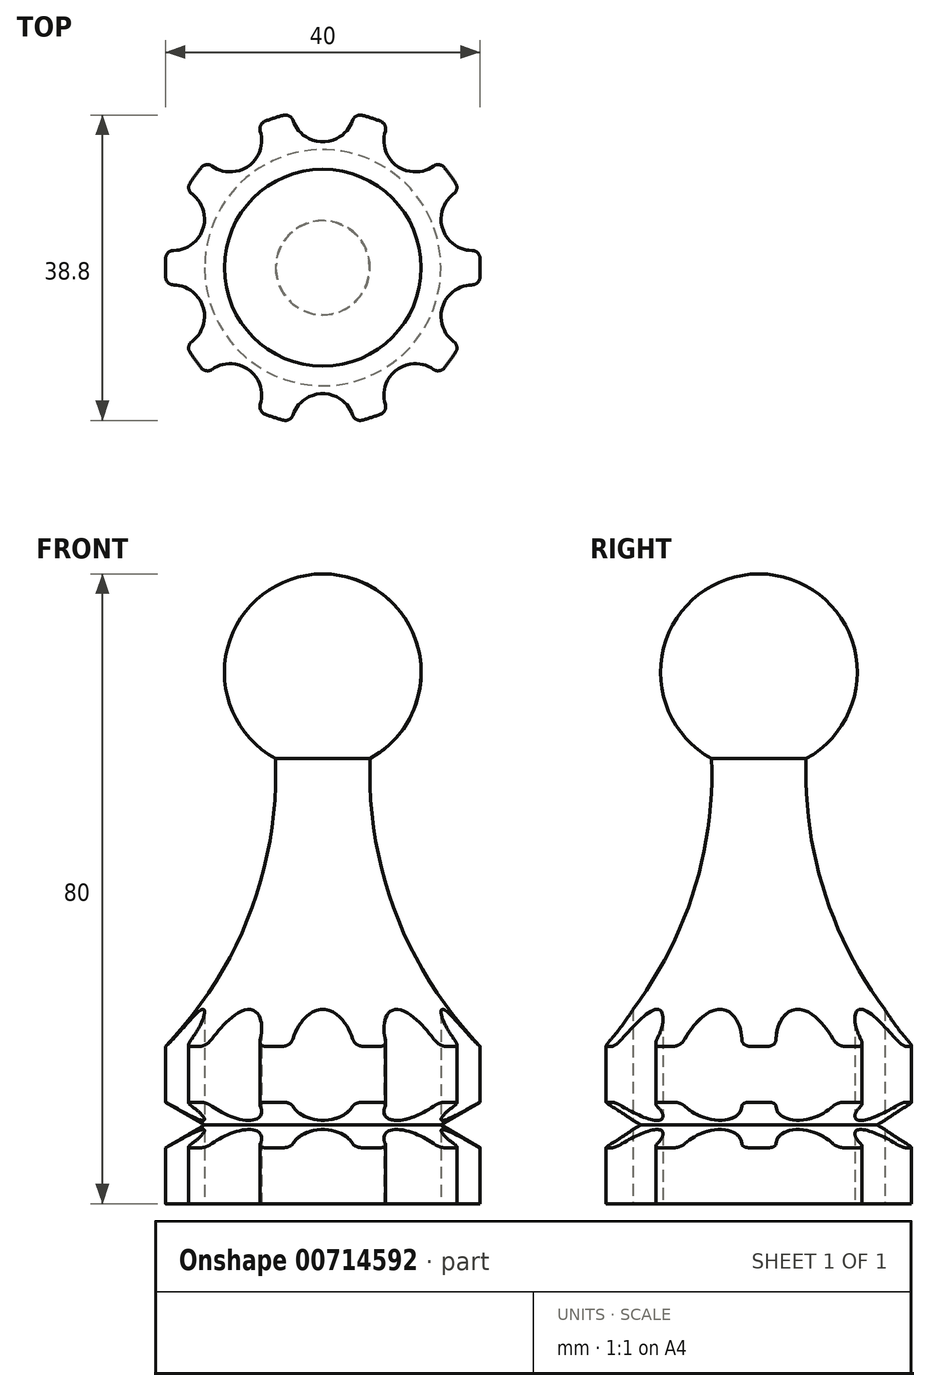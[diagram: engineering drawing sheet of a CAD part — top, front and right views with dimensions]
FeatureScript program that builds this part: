
annotation { "Feature Type Name" : "Feature", "Feature Type Description" : "" }
export const myFeature = defineFeature(function(context is Context, id is Id, definition is map)
    precondition{}
    {
        {
            var Q0;
            Q0=qCreatedBy(makeId("Front.planeOp"),FACE);
            var sketch = newSketch(context, id + "F0", { "sketchPlane" : qUnion([Q0])});
            skLineSegment(sketch, "E0", {"start": v(0, 80) * mm, "end": v(0, -103.84) * mm, "construction": true});
            skLineSegment(sketch, "E1", {"start": v(0, 0) * mm, "end": v(20, 0) * mm});
            skLineSegment(sketch, "E2", {"start": v(20, 0) * mm, "end": v(20, 12.89) * mm});
            skLineSegment(sketch, "E3", {"start": v(20, 12.89) * mm, "end": v(15, 10) * mm});
            skLineSegment(sketch, "E4", {"start": v(15, 10) * mm, "end": v(20, 7.11) * mm});
            skLineSegment(sketch, "E5", {"start": v(20, 7.11) * mm, "end": v(20, 20) * mm});
            skArc(sketch, "E6", {"start": v(6, 56.53) * mm, "mid": v(9.28, 36.84) * mm, "end": v(20, 20) * mm});
            skArc(sketch, "E7", {"start": v(6, 56.53) * mm, "mid": v(12.11, 70.6) * mm, "end": v(0, 80) * mm});
            skLineSegment(sketch, "E8", {"start": v(0, 80) * mm, "end": v(0, 0) * mm});
            skSolve(sketch);
        }
        {
            var Q0;
            Q0=makeQuery(id+"F0.imprint","IMPRINT",FACE,{"disambiguationData":[TD([[makeQuery(id+"F0.imprint","IMPRINT",EDGE,{"derivedFrom":sQuery(id+"F0.wireOp",EDGE,"E1")}),1.0]])]});
            var Q1;
            Q1=sQuery(id+"F0.wireOp",EDGE,"E8");
            revolve(context, id + "F1", {"surfaceOperationType" : NewSurfaceOperationType.NEW, "entities" : qUnion([Q0]), "axis" : qUnion([Q1]), "revolveType" : RevolveType.FULL, "oppositeDirection" : true});
        }
        {
            var Q0;
            Q0=makeQuery(id+"F1.opRevolve","SWEPT_FACE",FACE,{"disambiguationData":[OSD([sQuery(id+"F0.wireOp",EDGE,"E1")])]});
            var sketch = newSketch(context, id + "F2", { "sketchPlane" : qUnion([Q0])});
            skCircle(sketch, "E9", {"center": v(0, 20) * mm, "radius": 4 * mm});
            skCircle(sketch, "E10.1.0", {"center": v(-11.76, 16.18) * mm, "radius": 4 * mm});
            skCircle(sketch, "E10.2.0", {"center": v(-19.02, 6.18) * mm, "radius": 4 * mm});
            skCircle(sketch, "E10.3.0", {"center": v(-19.02, -6.18) * mm, "radius": 4 * mm});
            skCircle(sketch, "E10.4.0", {"center": v(-11.76, -16.18) * mm, "radius": 4 * mm});
            skCircle(sketch, "E10.5.0", {"center": v(0, -20) * mm, "radius": 4 * mm});
            skCircle(sketch, "E10.6.0", {"center": v(11.76, -16.18) * mm, "radius": 4 * mm});
            skCircle(sketch, "E10.7.0", {"center": v(19.02, -6.18) * mm, "radius": 4 * mm});
            skCircle(sketch, "E10.8.0", {"center": v(19.02, 6.18) * mm, "radius": 4 * mm});
            skCircle(sketch, "E10.9.0", {"center": v(11.76, 16.18) * mm, "radius": 4 * mm});
            skPoint(sketch, "E10.center", {"position": v(0, 0) * mm});
            skSolve(sketch);
        }
        {
            var Q0;
            Q0 = qSketchRegion(id + "F2", true);
            extrude(context, id + "F3", {"entities" : qUnion([Q0]), "operationType" : NewBodyOperationType.REMOVE, "oppositeDirection" : true, "depth" : 25 * mm, "offsetDistance" : 25 * mm});
        }
        {
            var Q0;
            Q0=makeQuery(id+"F3.boolean.opBoolean","INTERSECT",EDGE,{"disambiguationData":[OD(1.0)],"derivedFrom":[makeQuery(id+"F1.opRevolve","SWEPT_FACE",FACE,{"disambiguationData":[OSD([sQuery(id+"F0.wireOp",EDGE,"E5")])]}),makeQuery(id+"F3.opExtrude","SWEPT_FACE",FACE,{"disambiguationData":[OSD([sQuery(id+"F2.wireOp",EDGE,"E10.1.0")])]})]});
            var Q1;
            Q1=makeQuery(id+"F3.boolean.opBoolean","INTERSECT",EDGE,{"disambiguationData":[OD(0.0)],"derivedFrom":[makeQuery(id+"F1.opRevolve","SWEPT_FACE",FACE,{"disambiguationData":[OSD([sQuery(id+"F0.wireOp",EDGE,"E5")])]}),makeQuery(id+"F3.opExtrude","SWEPT_FACE",FACE,{"disambiguationData":[OSD([sQuery(id+"F2.wireOp",EDGE,"E10.2.0")])]})]});
            var Q2;
            Q2=makeQuery(id+"F3.boolean.opBoolean","INTERSECT",EDGE,{"disambiguationData":[OD(0.0)],"derivedFrom":[makeQuery(id+"F1.opRevolve","SWEPT_FACE",FACE,{"disambiguationData":[OSD([sQuery(id+"F0.wireOp",EDGE,"E5")])]}),makeQuery(id+"F3.opExtrude","SWEPT_FACE",FACE,{"disambiguationData":[OSD([sQuery(id+"F2.wireOp",EDGE,"E10.1.0")])]})]});
            var Q3;
            Q3=makeQuery(id+"F3.boolean.opBoolean","INTERSECT",EDGE,{"disambiguationData":[OD(0.0)],"derivedFrom":[makeQuery(id+"F1.opRevolve","SWEPT_FACE",FACE,{"disambiguationData":[OSD([sQuery(id+"F0.wireOp",EDGE,"E5")])]}),makeQuery(id+"F3.opExtrude","SWEPT_FACE",FACE,{"disambiguationData":[OSD([sQuery(id+"F2.wireOp",EDGE,"E9")])]})]});
            var Q4;
            Q4=makeQuery(id+"F3.boolean.opBoolean","INTERSECT",EDGE,{"disambiguationData":[OD(1.0)],"derivedFrom":[makeQuery(id+"F1.opRevolve","SWEPT_FACE",FACE,{"disambiguationData":[OSD([sQuery(id+"F0.wireOp",EDGE,"E5")])]}),makeQuery(id+"F3.opExtrude","SWEPT_FACE",FACE,{"disambiguationData":[OSD([sQuery(id+"F2.wireOp",EDGE,"E10.2.0")])]})]});
            var Q5;
            Q5=makeQuery(id+"F3.boolean.opBoolean","INTERSECT",EDGE,{"disambiguationData":[OD(0.0)],"derivedFrom":[makeQuery(id+"F1.opRevolve","SWEPT_FACE",FACE,{"disambiguationData":[OSD([sQuery(id+"F0.wireOp",EDGE,"E5")])]}),makeQuery(id+"F3.opExtrude","SWEPT_FACE",FACE,{"disambiguationData":[OSD([sQuery(id+"F2.wireOp",EDGE,"E10.3.0")])]})]});
            var Q6;
            Q6=makeQuery(id+"F3.boolean.opBoolean","INTERSECT",EDGE,{"disambiguationData":[OD(1.0)],"derivedFrom":[makeQuery(id+"F1.opRevolve","SWEPT_FACE",FACE,{"disambiguationData":[OSD([sQuery(id+"F0.wireOp",EDGE,"E5")])]}),makeQuery(id+"F3.opExtrude","SWEPT_FACE",FACE,{"disambiguationData":[OSD([sQuery(id+"F2.wireOp",EDGE,"E9")])]})]});
            var Q7;
            Q7=makeQuery(id+"F3.boolean.opBoolean","INTERSECT",EDGE,{"disambiguationData":[OD(0.0)],"derivedFrom":[makeQuery(id+"F1.opRevolve","SWEPT_FACE",FACE,{"disambiguationData":[OSD([sQuery(id+"F0.wireOp",EDGE,"E5")])]}),makeQuery(id+"F3.opExtrude","SWEPT_FACE",FACE,{"disambiguationData":[OSD([sQuery(id+"F2.wireOp",EDGE,"E10.9.0")])]})]});
            var Q8;
            Q8=makeQuery(id+"F3.boolean.opBoolean","INTERSECT",EDGE,{"disambiguationData":[OD(0.0)],"derivedFrom":[makeQuery(id+"F1.opRevolve","SWEPT_FACE",FACE,{"disambiguationData":[OSD([sQuery(id+"F0.wireOp",EDGE,"E5")])]}),makeQuery(id+"F3.opExtrude","SWEPT_FACE",FACE,{"disambiguationData":[OSD([sQuery(id+"F2.wireOp",EDGE,"E10.4.0")])]})]});
            var Q9;
            Q9=makeQuery(id+"F3.boolean.opBoolean","INTERSECT",EDGE,{"disambiguationData":[OD(1.0)],"derivedFrom":[makeQuery(id+"F1.opRevolve","SWEPT_FACE",FACE,{"disambiguationData":[OSD([sQuery(id+"F0.wireOp",EDGE,"E5")])]}),makeQuery(id+"F3.opExtrude","SWEPT_FACE",FACE,{"disambiguationData":[OSD([sQuery(id+"F2.wireOp",EDGE,"E10.4.0")])]})]});
            var Q10;
            Q10=makeQuery(id+"F3.boolean.opBoolean","INTERSECT",EDGE,{"disambiguationData":[OD(0.0)],"derivedFrom":[makeQuery(id+"F1.opRevolve","SWEPT_FACE",FACE,{"disambiguationData":[OSD([sQuery(id+"F0.wireOp",EDGE,"E5")])]}),makeQuery(id+"F3.opExtrude","SWEPT_FACE",FACE,{"disambiguationData":[OSD([sQuery(id+"F2.wireOp",EDGE,"E10.5.0")])]})]});
            var Q11;
            Q11=makeQuery(id+"F3.boolean.opBoolean","INTERSECT",EDGE,{"disambiguationData":[OD(1.0)],"derivedFrom":[makeQuery(id+"F1.opRevolve","SWEPT_FACE",FACE,{"disambiguationData":[OSD([sQuery(id+"F0.wireOp",EDGE,"E5")])]}),makeQuery(id+"F3.opExtrude","SWEPT_FACE",FACE,{"disambiguationData":[OSD([sQuery(id+"F2.wireOp",EDGE,"E10.5.0")])]})]});
            var Q12;
            Q12=makeQuery(id+"F3.boolean.opBoolean","INTERSECT",EDGE,{"disambiguationData":[OD(0.0)],"derivedFrom":[makeQuery(id+"F1.opRevolve","SWEPT_FACE",FACE,{"disambiguationData":[OSD([sQuery(id+"F0.wireOp",EDGE,"E5")])]}),makeQuery(id+"F3.opExtrude","SWEPT_FACE",FACE,{"disambiguationData":[OSD([sQuery(id+"F2.wireOp",EDGE,"E10.6.0")])]})]});
            var Q13;
            Q13=makeQuery(id+"F3.boolean.opBoolean","INTERSECT",EDGE,{"disambiguationData":[OD(1.0)],"derivedFrom":[makeQuery(id+"F1.opRevolve","SWEPT_FACE",FACE,{"disambiguationData":[OSD([sQuery(id+"F0.wireOp",EDGE,"E5")])]}),makeQuery(id+"F3.opExtrude","SWEPT_FACE",FACE,{"disambiguationData":[OSD([sQuery(id+"F2.wireOp",EDGE,"E10.6.0")])]})]});
            var Q14;
            Q14=makeQuery(id+"F3.boolean.opBoolean","INTERSECT",EDGE,{"disambiguationData":[OD(0.0)],"derivedFrom":[makeQuery(id+"F1.opRevolve","SWEPT_FACE",FACE,{"disambiguationData":[OSD([sQuery(id+"F0.wireOp",EDGE,"E5")])]}),makeQuery(id+"F3.opExtrude","SWEPT_FACE",FACE,{"disambiguationData":[OSD([sQuery(id+"F2.wireOp",EDGE,"E10.7.0")])]})]});
            var Q15;
            Q15=makeQuery(id+"F3.boolean.opBoolean","INTERSECT",EDGE,{"disambiguationData":[OD(1.0)],"derivedFrom":[makeQuery(id+"F1.opRevolve","SWEPT_FACE",FACE,{"disambiguationData":[OSD([sQuery(id+"F0.wireOp",EDGE,"E5")])]}),makeQuery(id+"F3.opExtrude","SWEPT_FACE",FACE,{"disambiguationData":[OSD([sQuery(id+"F2.wireOp",EDGE,"E10.7.0")])]})]});
            var Q16;
            Q16=makeQuery(id+"F3.boolean.opBoolean","INTERSECT",EDGE,{"disambiguationData":[OD(0.0)],"derivedFrom":[makeQuery(id+"F1.opRevolve","SWEPT_FACE",FACE,{"disambiguationData":[OSD([sQuery(id+"F0.wireOp",EDGE,"E5")])]}),makeQuery(id+"F3.opExtrude","SWEPT_FACE",FACE,{"disambiguationData":[OSD([sQuery(id+"F2.wireOp",EDGE,"E10.8.0")])]})]});
            var Q17;
            Q17=makeQuery(id+"F3.boolean.opBoolean","INTERSECT",EDGE,{"disambiguationData":[OD(1.0)],"derivedFrom":[makeQuery(id+"F1.opRevolve","SWEPT_FACE",FACE,{"disambiguationData":[OSD([sQuery(id+"F0.wireOp",EDGE,"E5")])]}),makeQuery(id+"F3.opExtrude","SWEPT_FACE",FACE,{"disambiguationData":[OSD([sQuery(id+"F2.wireOp",EDGE,"E10.8.0")])]})]});
            var Q18;
            Q18=makeQuery(id+"F3.boolean.opBoolean","INTERSECT",EDGE,{"disambiguationData":[OD(1.0)],"derivedFrom":[makeQuery(id+"F1.opRevolve","SWEPT_FACE",FACE,{"disambiguationData":[OSD([sQuery(id+"F0.wireOp",EDGE,"E5")])]}),makeQuery(id+"F3.opExtrude","SWEPT_FACE",FACE,{"disambiguationData":[OSD([sQuery(id+"F2.wireOp",EDGE,"E10.9.0")])]})]});
            var Q19;
            Q19=makeQuery(id+"F3.boolean.opBoolean","INTERSECT",EDGE,{"disambiguationData":[OD(1.0)],"derivedFrom":[makeQuery(id+"F1.opRevolve","SWEPT_FACE",FACE,{"disambiguationData":[OSD([sQuery(id+"F0.wireOp",EDGE,"E5")])]}),makeQuery(id+"F3.opExtrude","SWEPT_FACE",FACE,{"disambiguationData":[OSD([sQuery(id+"F2.wireOp",EDGE,"E10.3.0")])]})]});
            fillet(context, id + "F4", {"entities" : qUnion([Q0, Q1, Q2, Q3, Q4, Q5, Q6, Q7, Q8, Q9, Q10, Q11, Q12, Q13, Q14, Q15, Q16, Q17, Q18, Q19]), "radius" : 1 * mm, "tangentPropagation" : true, "allowEdgeOverflow" : false});
        }
        {
            var Q0;
            Q0=makeQuery(id+"F3.boolean.opBoolean","INTERSECT",EDGE,{"disambiguationData":[OD(0.0)],"derivedFrom":[makeQuery(id+"F1.opRevolve","SWEPT_FACE",FACE,{"disambiguationData":[OSD([sQuery(id+"F0.wireOp",EDGE,"E2")])]}),makeQuery(id+"F3.opExtrude","SWEPT_FACE",FACE,{"disambiguationData":[OSD([sQuery(id+"F2.wireOp",EDGE,"E10.6.0")])]})]});
            var Q1;
            Q1=makeQuery(id+"F3.boolean.opBoolean","INTERSECT",EDGE,{"disambiguationData":[OD(1.0)],"derivedFrom":[makeQuery(id+"F1.opRevolve","SWEPT_FACE",FACE,{"disambiguationData":[OSD([sQuery(id+"F0.wireOp",EDGE,"E2")])]}),makeQuery(id+"F3.opExtrude","SWEPT_FACE",FACE,{"disambiguationData":[OSD([sQuery(id+"F2.wireOp",EDGE,"E10.6.0")])]})]});
            var Q2;
            Q2=makeQuery(id+"F3.boolean.opBoolean","INTERSECT",EDGE,{"disambiguationData":[OD(0.0)],"derivedFrom":[makeQuery(id+"F1.opRevolve","SWEPT_FACE",FACE,{"disambiguationData":[OSD([sQuery(id+"F0.wireOp",EDGE,"E2")])]}),makeQuery(id+"F3.opExtrude","SWEPT_FACE",FACE,{"disambiguationData":[OSD([sQuery(id+"F2.wireOp",EDGE,"E10.7.0")])]})]});
            var Q3;
            Q3=makeQuery(id+"F3.boolean.opBoolean","INTERSECT",EDGE,{"disambiguationData":[OD(1.0)],"derivedFrom":[makeQuery(id+"F1.opRevolve","SWEPT_FACE",FACE,{"disambiguationData":[OSD([sQuery(id+"F0.wireOp",EDGE,"E2")])]}),makeQuery(id+"F3.opExtrude","SWEPT_FACE",FACE,{"disambiguationData":[OSD([sQuery(id+"F2.wireOp",EDGE,"E10.7.0")])]})]});
            var Q4;
            Q4=makeQuery(id+"F3.boolean.opBoolean","INTERSECT",EDGE,{"disambiguationData":[OD(1.0)],"derivedFrom":[makeQuery(id+"F1.opRevolve","SWEPT_FACE",FACE,{"disambiguationData":[OSD([sQuery(id+"F0.wireOp",EDGE,"E2")])]}),makeQuery(id+"F3.opExtrude","SWEPT_FACE",FACE,{"disambiguationData":[OSD([sQuery(id+"F2.wireOp",EDGE,"E10.5.0")])]})]});
            var Q5;
            Q5=makeQuery(id+"F3.boolean.opBoolean","INTERSECT",EDGE,{"disambiguationData":[OD(0.0)],"derivedFrom":[makeQuery(id+"F1.opRevolve","SWEPT_FACE",FACE,{"disambiguationData":[OSD([sQuery(id+"F0.wireOp",EDGE,"E2")])]}),makeQuery(id+"F3.opExtrude","SWEPT_FACE",FACE,{"disambiguationData":[OSD([sQuery(id+"F2.wireOp",EDGE,"E10.5.0")])]})]});
            var Q6;
            Q6=makeQuery(id+"F3.boolean.opBoolean","INTERSECT",EDGE,{"disambiguationData":[OD(1.0)],"derivedFrom":[makeQuery(id+"F1.opRevolve","SWEPT_FACE",FACE,{"disambiguationData":[OSD([sQuery(id+"F0.wireOp",EDGE,"E2")])]}),makeQuery(id+"F3.opExtrude","SWEPT_FACE",FACE,{"disambiguationData":[OSD([sQuery(id+"F2.wireOp",EDGE,"E10.4.0")])]})]});
            var Q7;
            Q7=makeQuery(id+"F3.boolean.opBoolean","INTERSECT",EDGE,{"disambiguationData":[OD(0.0)],"derivedFrom":[makeQuery(id+"F1.opRevolve","SWEPT_FACE",FACE,{"disambiguationData":[OSD([sQuery(id+"F0.wireOp",EDGE,"E2")])]}),makeQuery(id+"F3.opExtrude","SWEPT_FACE",FACE,{"disambiguationData":[OSD([sQuery(id+"F2.wireOp",EDGE,"E10.4.0")])]})]});
            var Q8;
            Q8=makeQuery(id+"F3.boolean.opBoolean","INTERSECT",EDGE,{"disambiguationData":[OD(1.0)],"derivedFrom":[makeQuery(id+"F1.opRevolve","SWEPT_FACE",FACE,{"disambiguationData":[OSD([sQuery(id+"F0.wireOp",EDGE,"E2")])]}),makeQuery(id+"F3.opExtrude","SWEPT_FACE",FACE,{"disambiguationData":[OSD([sQuery(id+"F2.wireOp",EDGE,"E10.3.0")])]})]});
            var Q9;
            Q9=makeQuery(id+"F3.boolean.opBoolean","INTERSECT",EDGE,{"disambiguationData":[OD(0.0)],"derivedFrom":[makeQuery(id+"F1.opRevolve","SWEPT_FACE",FACE,{"disambiguationData":[OSD([sQuery(id+"F0.wireOp",EDGE,"E2")])]}),makeQuery(id+"F3.opExtrude","SWEPT_FACE",FACE,{"disambiguationData":[OSD([sQuery(id+"F2.wireOp",EDGE,"E10.3.0")])]})]});
            var Q10;
            Q10=makeQuery(id+"F3.boolean.opBoolean","INTERSECT",EDGE,{"disambiguationData":[OD(0.0)],"derivedFrom":[makeQuery(id+"F1.opRevolve","SWEPT_FACE",FACE,{"disambiguationData":[OSD([sQuery(id+"F0.wireOp",EDGE,"E2")])]}),makeQuery(id+"F3.opExtrude","SWEPT_FACE",FACE,{"disambiguationData":[OSD([sQuery(id+"F2.wireOp",EDGE,"E10.8.0")])]})]});
            var Q11;
            Q11=makeQuery(id+"F3.boolean.opBoolean","INTERSECT",EDGE,{"disambiguationData":[OD(1.0)],"derivedFrom":[makeQuery(id+"F1.opRevolve","SWEPT_FACE",FACE,{"disambiguationData":[OSD([sQuery(id+"F0.wireOp",EDGE,"E2")])]}),makeQuery(id+"F3.opExtrude","SWEPT_FACE",FACE,{"disambiguationData":[OSD([sQuery(id+"F2.wireOp",EDGE,"E10.8.0")])]})]});
            var Q12;
            Q12=makeQuery(id+"F3.boolean.opBoolean","INTERSECT",EDGE,{"disambiguationData":[OD(1.0)],"derivedFrom":[makeQuery(id+"F1.opRevolve","SWEPT_FACE",FACE,{"disambiguationData":[OSD([sQuery(id+"F0.wireOp",EDGE,"E2")])]}),makeQuery(id+"F3.opExtrude","SWEPT_FACE",FACE,{"disambiguationData":[OSD([sQuery(id+"F2.wireOp",EDGE,"E10.9.0")])]})]});
            var Q13;
            Q13=makeQuery(id+"F3.boolean.opBoolean","INTERSECT",EDGE,{"disambiguationData":[OD(0.0)],"derivedFrom":[makeQuery(id+"F1.opRevolve","SWEPT_FACE",FACE,{"disambiguationData":[OSD([sQuery(id+"F0.wireOp",EDGE,"E2")])]}),makeQuery(id+"F3.opExtrude","SWEPT_FACE",FACE,{"disambiguationData":[OSD([sQuery(id+"F2.wireOp",EDGE,"E10.9.0")])]})]});
            var Q14;
            Q14=makeQuery(id+"F3.boolean.opBoolean","INTERSECT",EDGE,{"disambiguationData":[OD(1.0)],"derivedFrom":[makeQuery(id+"F1.opRevolve","SWEPT_FACE",FACE,{"disambiguationData":[OSD([sQuery(id+"F0.wireOp",EDGE,"E2")])]}),makeQuery(id+"F3.opExtrude","SWEPT_FACE",FACE,{"disambiguationData":[OSD([sQuery(id+"F2.wireOp",EDGE,"E9")])]})]});
            var Q15;
            Q15=makeQuery(id+"F3.boolean.opBoolean","INTERSECT",EDGE,{"disambiguationData":[OD(0.0)],"derivedFrom":[makeQuery(id+"F1.opRevolve","SWEPT_FACE",FACE,{"disambiguationData":[OSD([sQuery(id+"F0.wireOp",EDGE,"E2")])]}),makeQuery(id+"F3.opExtrude","SWEPT_FACE",FACE,{"disambiguationData":[OSD([sQuery(id+"F2.wireOp",EDGE,"E9")])]})]});
            var Q16;
            Q16=makeQuery(id+"F3.boolean.opBoolean","INTERSECT",EDGE,{"disambiguationData":[OD(0.0)],"derivedFrom":[makeQuery(id+"F1.opRevolve","SWEPT_FACE",FACE,{"disambiguationData":[OSD([sQuery(id+"F0.wireOp",EDGE,"E2")])]}),makeQuery(id+"F3.opExtrude","SWEPT_FACE",FACE,{"disambiguationData":[OSD([sQuery(id+"F2.wireOp",EDGE,"E10.1.0")])]})]});
            var Q17;
            Q17=makeQuery(id+"F3.boolean.opBoolean","INTERSECT",EDGE,{"disambiguationData":[OD(1.0)],"derivedFrom":[makeQuery(id+"F1.opRevolve","SWEPT_FACE",FACE,{"disambiguationData":[OSD([sQuery(id+"F0.wireOp",EDGE,"E2")])]}),makeQuery(id+"F3.opExtrude","SWEPT_FACE",FACE,{"disambiguationData":[OSD([sQuery(id+"F2.wireOp",EDGE,"E10.1.0")])]})]});
            var Q18;
            Q18=makeQuery(id+"F3.boolean.opBoolean","INTERSECT",EDGE,{"disambiguationData":[OD(0.0)],"derivedFrom":[makeQuery(id+"F1.opRevolve","SWEPT_FACE",FACE,{"disambiguationData":[OSD([sQuery(id+"F0.wireOp",EDGE,"E2")])]}),makeQuery(id+"F3.opExtrude","SWEPT_FACE",FACE,{"disambiguationData":[OSD([sQuery(id+"F2.wireOp",EDGE,"E10.2.0")])]})]});
            var Q19;
            Q19=makeQuery(id+"F3.boolean.opBoolean","INTERSECT",EDGE,{"disambiguationData":[OD(1.0)],"derivedFrom":[makeQuery(id+"F1.opRevolve","SWEPT_FACE",FACE,{"disambiguationData":[OSD([sQuery(id+"F0.wireOp",EDGE,"E2")])]}),makeQuery(id+"F3.opExtrude","SWEPT_FACE",FACE,{"disambiguationData":[OSD([sQuery(id+"F2.wireOp",EDGE,"E10.2.0")])]})]});
            fillet(context, id + "F5", {"entities" : qUnion([Q0, Q1, Q2, Q3, Q4, Q5, Q6, Q7, Q8, Q9, Q10, Q11, Q12, Q13, Q14, Q15, Q16, Q17, Q18, Q19]), "radius" : 1 * mm, "tangentPropagation" : true, "allowEdgeOverflow" : false});
        }
    });
